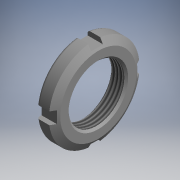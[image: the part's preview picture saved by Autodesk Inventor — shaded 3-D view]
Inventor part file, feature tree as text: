
AUTODESK INVENTOR PART (.ipt)
format: ipt  version: 2017.3 (Build 213256000, 256)  size: 159,232 bytes
history: native  units: mm (DEFAULTED — no unit token found)
features: other x28, sketch x2, revolve x1, thread x1, extrude x1
ambient origin geometry x8: Origin, YZ Plane, XZ Plane, XY Plane, X Axis, Y Axis, Z Axis, Center Point
bodies: Solid1 (feature_tree)
feature tree (33):
  revolve  "Revolution1"  [1 undecoded]
  thread  "Thread1"  [1 undecoded]
  extrude  "Extrusion1"  [1 undecoded]
  other  "km_XY"
  other  "km_YZ"
  other  "km_ZX"
  other  "km_X"
  other  "km_Y"
  other  "km_Z"
  other  "km_Center"
  other  "km2_XY"
  other  "km2_YZ"
  other  "km2_ZX"
  other  "km2_X"
  other  "km2_Y"
  other  "km2_Z"
  other  "km2_Center"
  other  "ln_XY"
  other  "ln_YZ"
  other  "ln_ZX"
  other  "ln_X"
  other  "ln_Y"
  other  "ln_Z"
  other  "ln_Center"
  other  "nut_XY"
  other  "nut_YZ"
  other  "nut_ZX"
  other  "nut_X"
  other  "nut_Y"
  other  "nut_Z"
  other  "nut_Center"
  sketch  "Sketch_3"  dims[d0=360.0deg d1=5.376mm d2=0.0mm d3=14.0mm d4=0.0mm]
  sketch  "Sketch_6"  dims[d5=0.0mm d6=0.0mm d7=0.0mm]
note: 3 required parameter values undecoded (feature->parameter linkage not recoverable at this tier; creation-order binding heuristic only, values carry confidence <= 0.55)